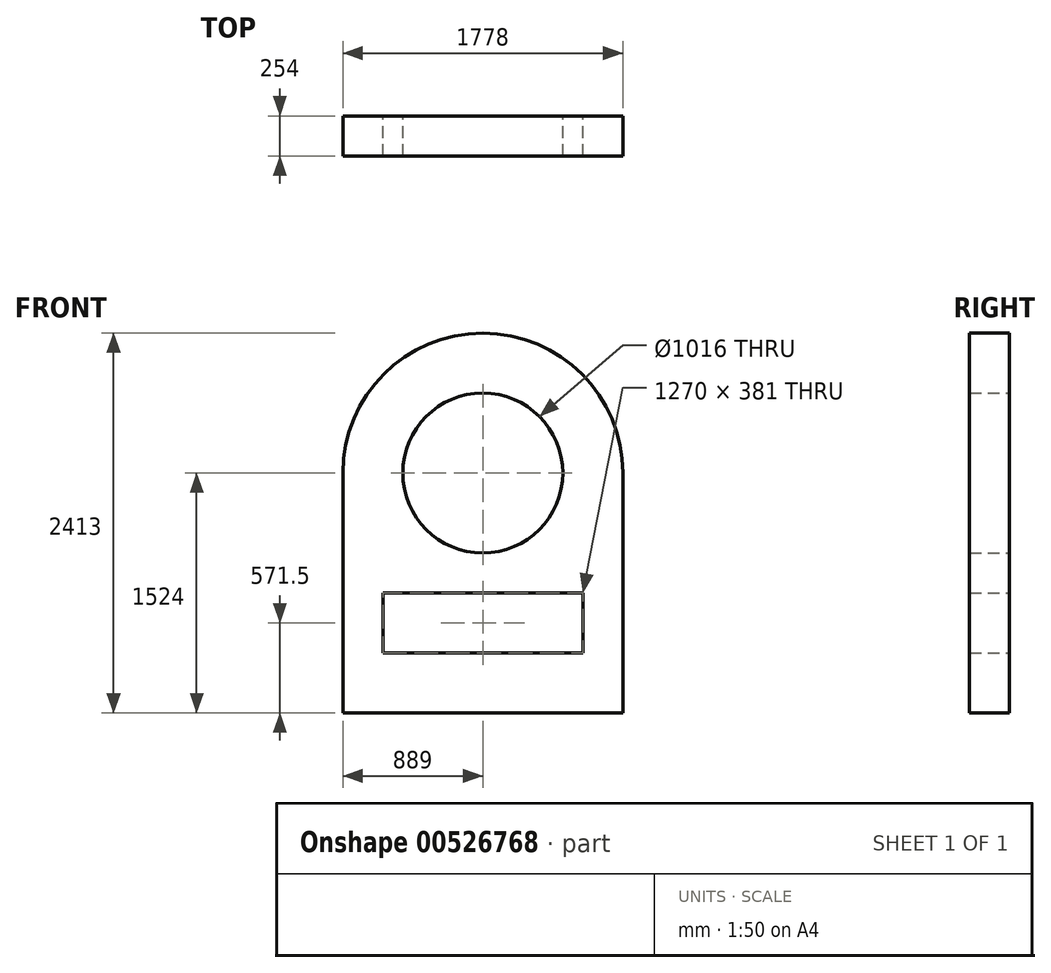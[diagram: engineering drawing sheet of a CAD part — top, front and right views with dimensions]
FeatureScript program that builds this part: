
annotation { "Feature Type Name" : "Feature", "Feature Type Description" : "" }
export const myFeature = defineFeature(function(context is Context, id is Id, definition is map)
    precondition{}
    {
        {
            var Q0;
            Q0=qCreatedBy(makeId("Front.planeOp"),FACE);
            var sketch = newSketch(context, id + "F0", { "sketchPlane" : qUnion([Q0])});
            skLineSegment(sketch, "E0", {"start": v(0, 0) * mm, "end": v(1778, 0) * mm});
            skLineSegment(sketch, "E1", {"start": v(0, 0) * mm, "end": v(0, 1524) * mm});
            skLineSegment(sketch, "E2", {"start": v(1778, 0) * mm, "end": v(1778, 1524) * mm});
            skLineSegment(sketch, "E3.bottom", {"start": v(254, 762) * mm, "end": v(1524, 762) * mm});
            skLineSegment(sketch, "E3.top", {"start": v(254, 381) * mm, "end": v(1524, 381) * mm});
            skLineSegment(sketch, "E3.left", {"start": v(254, 762) * mm, "end": v(254, 381) * mm});
            skLineSegment(sketch, "E3.right", {"start": v(1524, 762) * mm, "end": v(1524, 381) * mm});
            skArc(sketch, "E4", {"start": v(1778, 1524) * mm, "mid": v(889, 2413) * mm, "end": v(0, 1524) * mm});
            skCircle(sketch, "E5", {"center": v(889, 1524) * mm, "radius": 508 * mm});
            skSolve(sketch);
        }
        {
            var Q0;
            Q0=makeQuery(id+"F0.imprint","IMPRINT",FACE,{"disambiguationData":[TD([[makeQuery(id+"F0.imprint","IMPRINT",EDGE,{"derivedFrom":sQuery(id+"F0.wireOp",EDGE,"E0")}),1.0]])]});
            extrude(context, id + "F1", {"entities" : qUnion([Q0]), "depth" : 254 * mm, "offsetDistance" : 25.4 * mm});
        }
    });
